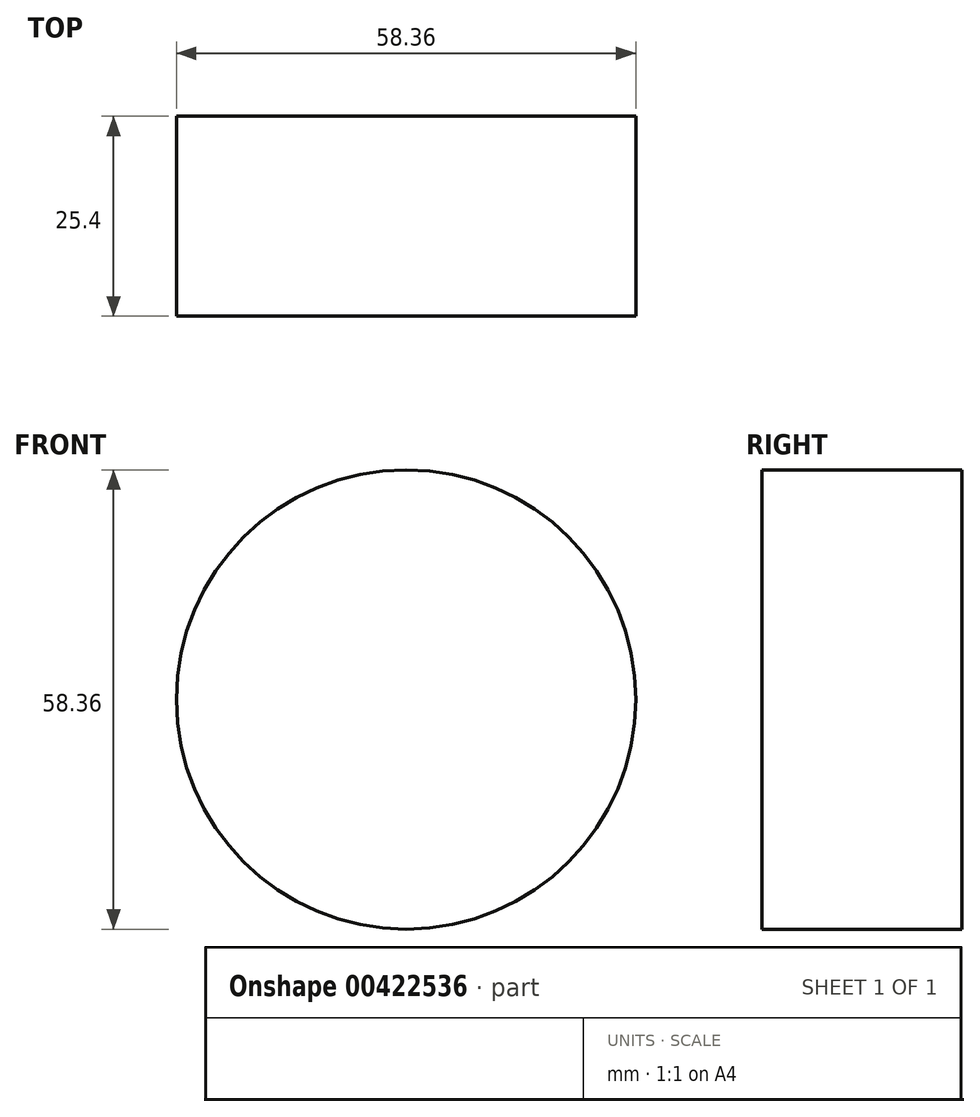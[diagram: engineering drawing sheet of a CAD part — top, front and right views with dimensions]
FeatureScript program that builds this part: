
annotation { "Feature Type Name" : "Feature", "Feature Type Description" : "" }
export const myFeature = defineFeature(function(context is Context, id is Id, definition is map)
    precondition{}
    {
        {
            var Q0;
            Q0=qCreatedBy(makeId("Front.planeOp"),FACE);
            var sketch = newSketch(context, id + "F0", { "sketchPlane" : qUnion([Q0])});
            skCircle(sketch, "E0", {"center": v(0, 0) * mm, "radius": 29.18 * mm});
            skSolve(sketch);
        }
        {
            var Q0;
            Q0 = qSketchRegion(id + "F0", true);
            extrude(context, id + "F1", {"entities" : qUnion([Q0]), "depth" : 25.4 * mm});
        }
    });
